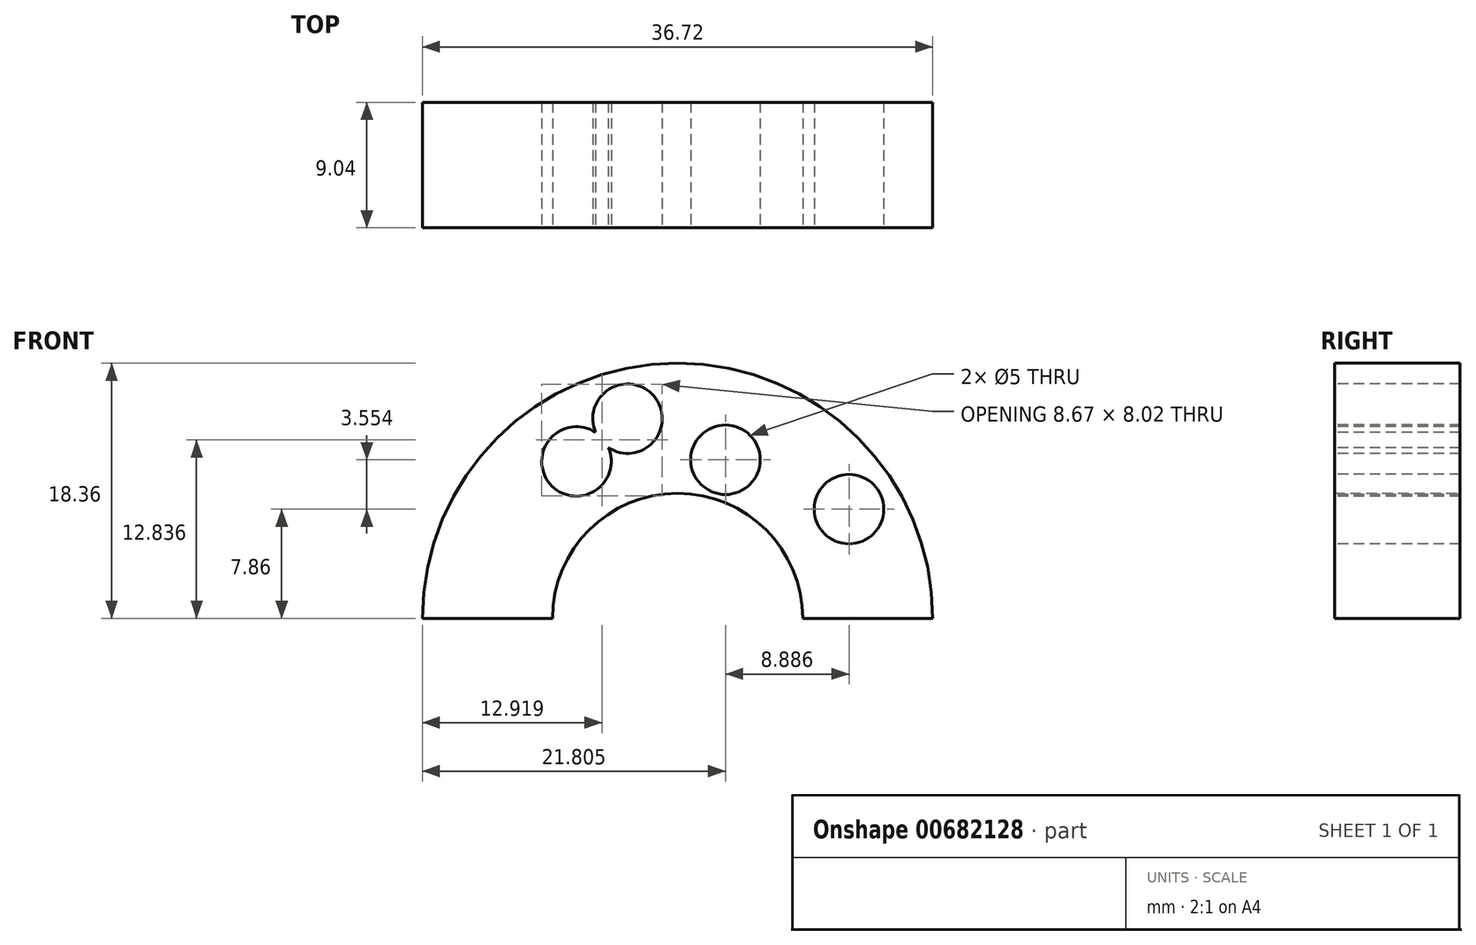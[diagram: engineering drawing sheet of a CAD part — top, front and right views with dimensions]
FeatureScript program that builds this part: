
annotation { "Feature Type Name" : "Feature", "Feature Type Description" : "" }
export const myFeature = defineFeature(function(context is Context, id is Id, definition is map)
    precondition{}
    {
        {
            var Q0;
            Q0=qCreatedBy(makeId("Top.planeOp"),FACE);
            var sketch = newSketch(context, id + "F0", { "sketchPlane" : qUnion([Q0])});
            skLineSegment(sketch, "E0", {"start": v(0, 37.97) * mm, "end": v(0, -34.03) * mm, "construction": true});
            skLineSegment(sketch, "E1.bottom", {"start": v(18.36, 4.52) * mm, "end": v(9, 4.52) * mm});
            skLineSegment(sketch, "E1.top", {"start": v(18.36, -4.52) * mm, "end": v(9, -4.52) * mm});
            skLineSegment(sketch, "E1.left", {"start": v(18.36, 4.52) * mm, "end": v(18.36, -4.52) * mm});
            skLineSegment(sketch, "E1.right", {"start": v(9, 4.52) * mm, "end": v(9, -4.52) * mm});
            skPoint(sketch, "E1.middle", {"position": v(13.68, 0) * mm});
            skSolve(sketch);
        }
        {
            var Q0;
            Q0 = qSketchRegion(id + "F0", true);
            var Q1;
            Q1=sQuery(id+"F0.wireOp",EDGE,"E0");
            revolve(context, id + "F1", {"entities" : qUnion([Q0]), "axis" : qUnion([Q1]), "revolveType" : RevolveType.ONE_DIRECTION, "angle" : 180 * degree});
        }
        {
            var Q0;
            Q0=makeQuery(id+"F1.opRevolve","SWEPT_FACE",FACE,{"disambiguationData":[OSD([sQuery(id+"F0.wireOp",EDGE,"E1.top")])]});
            var sketch = newSketch(context, id + "F2", { "sketchPlane" : qUnion([Q0])});
            skPoint(sketch, "E2", {"position": v(-7.28, 11.3) * mm});
            skPoint(sketch, "E3", {"position": v(-3.6, 14.38) * mm});
            skPoint(sketch, "E4", {"position": v(12.33, 7.86) * mm});
            skPoint(sketch, "E5", {"position": v(3.45, 11.41) * mm});
            skSolve(sketch);
        }
        {
            var Q0;
            Q0=sQuery(id+"F2.wireOp",VERTEX,"E2");
            var Q1;
            Q1=sQuery(id+"F2.wireOp",VERTEX,"E3");
            var Q2;
            Q2=sQuery(id+"F2.wireOp",VERTEX,"E5");
            var Q3;
            Q3=sQuery(id+"F2.wireOp",VERTEX,"E4");
            var Q4;
            Q4=makeQuery(id+"F1.opRevolve","SWEPT_BODY",BODY,{"disambiguationData":[OSD([sQuery(id+"F0.wireOp",EDGE,"E1.bottom"),sQuery(id+"F0.wireOp",EDGE,"E1.top"),sQuery(id+"F0.wireOp",EDGE,"E1.left"),sQuery(id+"F0.wireOp",EDGE,"E1.right")])]});
            hole(context, id + "F3", {"style" : HoleStyle.SIMPLE, "endStyle" : HoleEndStyle.THROUGH, "holeDiameter" : 5 * mm, "majorDiameter" : 5 * mm, "isTappedThrough" : true, "tappedDepth" : 12 * mm, "tapClearance" : 3, "locations" : qUnion([Q0, Q1, Q2, Q3]), "scope" : qUnion([Q4])});
        }
    });
